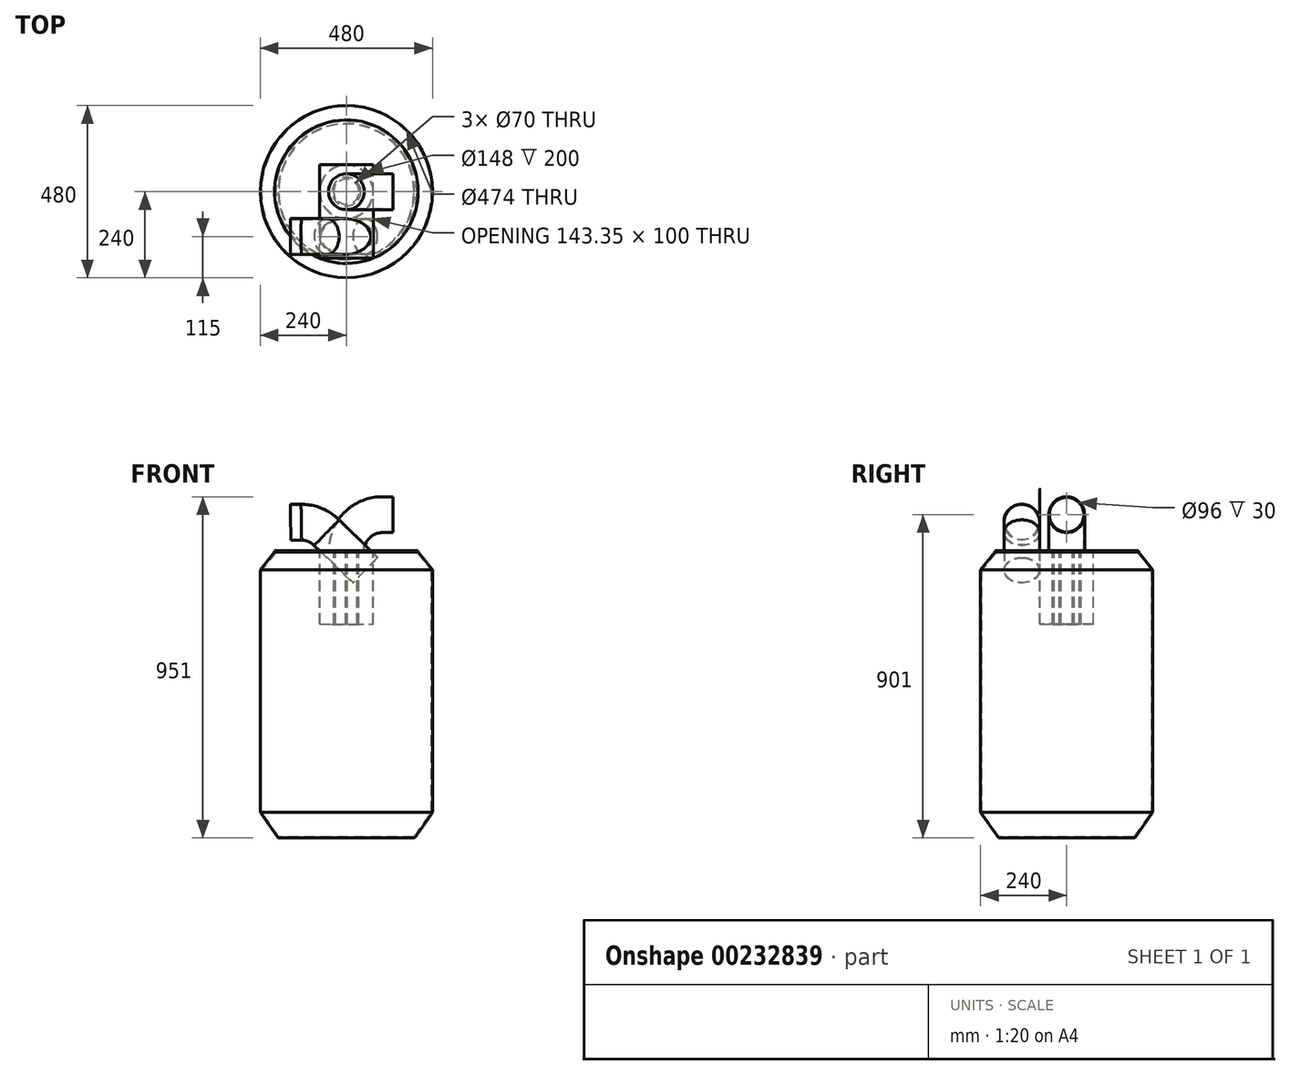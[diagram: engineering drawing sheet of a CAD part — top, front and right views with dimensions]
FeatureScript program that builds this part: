
annotation { "Feature Type Name" : "Feature", "Feature Type Description" : "" }
export const myFeature = defineFeature(function(context is Context, id is Id, definition is map)
    precondition{}
    {
        {
            assignVariable(context, id + "F0", {"name" : "FilterHeight", "anyValue" : 200});
        }
        {
            var Q0;
            Q0=qCreatedBy(makeId("Top.planeOp"),FACE);
            var sketch = newSketch(context, id + "F1", { "sketchPlane" : qUnion([Q0])});
            skCircle(sketch, "E0", {"center": v(0, 0) * mm, "radius": 200 * mm});
            skCircle(sketch, "E1", {"center": v(0, 0) * mm, "radius": 35 * mm});
            skSolve(sketch);
        }
        {
            var Q0;
            Q0=qSketchRegion(id+"F1",true);
            extrude(context, id + "F2", {"entities" : qUnion([Q0]), "depth" : 3 * mm});
        }
        {
            var Q0;
            Q0=makeQuery(id+"F2.opExtrude","CAP_FACE",FACE,{"disambiguationData":[OSD([sQuery(id+"F1.wireOp",EDGE,"E0"),sQuery(id+"F1.wireOp",EDGE,"E1")])],"isStart":true});
            var sketch = newSketch(context, id + "F3", { "sketchPlane" : qUnion([Q0])});
            skLineSegment(sketch, "E2.bottom", {"start": v(75, -75) * mm, "end": v(-75, -75) * mm});
            skLineSegment(sketch, "E2.top", {"start": v(75, 75) * mm, "end": v(-75, 75) * mm});
            skLineSegment(sketch, "E2.left", {"start": v(75, -75) * mm, "end": v(75, 75) * mm});
            skLineSegment(sketch, "E2.right", {"start": v(-75, -75) * mm, "end": v(-75, 75) * mm});
            skPoint(sketch, "E2.middle", {"position": v(0, 0) * mm});
            skCircle(sketch, "E3.0", {"center": v(0, 0) * mm, "radius": 35 * mm});
            skLineSegment(sketch, "E4.top", {"start": v(75, 185.4) * mm, "end": v(-75, 185.4) * mm});
            skLineSegment(sketch, "E4.left", {"start": v(75, 75) * mm, "end": v(75, 185.4) * mm});
            skLineSegment(sketch, "E4.right", {"start": v(-75, 75) * mm, "end": v(-75, 185.4) * mm});
            skSolve(sketch);
        }
        {
            var Q0;
            Q0=qSketchRegion(id+"F3",true);
            extrude(context, id + "F4", {"entities" : qUnion([Q0]), "depth" : 1 * mm});
        }
        {
            var Q0;
            Q0=makeQuery(id+"F4.opExtrude","CAP_FACE",FACE,{"disambiguationData":[OSD([sQuery(id+"F3.wireOp",EDGE,"E2.bottom"),sQuery(id+"F3.wireOp",EDGE,"E2.top"),sQuery(id+"F3.wireOp",EDGE,"E2.left"),sQuery(id+"F3.wireOp",EDGE,"E2.right"),sQuery(id+"F3.wireOp",EDGE,"E3.0")])],"isStart":false});
            var sketch = newSketch(context, id + "F5", { "sketchPlane" : qUnion([Q0])});
            skCircle(sketch, "E5", {"center": v(0, 37.5) * mm, "radius": 2.5 * mm});
            skCircle(sketch, "E6.1.0", {"center": v(-32.48, 18.75) * mm, "radius": 2.5 * mm});
            skCircle(sketch, "E6.2.0", {"center": v(-32.48, -18.75) * mm, "radius": 2.5 * mm});
            skCircle(sketch, "E6.3.0", {"center": v(0, -37.5) * mm, "radius": 2.5 * mm});
            skCircle(sketch, "E6.4.0", {"center": v(32.48, -18.75) * mm, "radius": 2.5 * mm});
            skCircle(sketch, "E6.5.0", {"center": v(32.48, 18.75) * mm, "radius": 2.5 * mm});
            skPoint(sketch, "E6.center", {"position": v(0, 0) * mm});
            skSolve(sketch);
        }
        {
            var Q0;
            Q0=qSketchRegion(id+"F5",true);
            extrude(context, id + "F6", {"entities" : qUnion([Q0]), "depth" : (getVariable(context, 'FilterHeight')) * mm});
        }
        {
            var Q0;
            Q0=makeQuery(id+"F6.opExtrude","CAP_FACE",FACE,{"disambiguationData":[OSD([sQuery(id+"F5.wireOp",EDGE,"E5")])],"isStart":false});
            var sketch = newSketch(context, id + "F7", { "sketchPlane" : qUnion([Q0])});
            skCircle(sketch, "E7", {"center": v(0, 0) * mm, "radius": 40 * mm});
            skSolve(sketch);
        }
        {
            var Q0;
            Q0=qSketchRegion(id+"F7",true);
            extrude(context, id + "F8", {"entities" : qUnion([Q0]), "depth" : 1 * mm});
        }
        {
            var Q0;
            Q0=makeQuery(id+"F4.opExtrude","CAP_FACE",FACE,{"disambiguationData":[OSD([sQuery(id+"F3.wireOp",EDGE,"E2.bottom"),sQuery(id+"F3.wireOp",EDGE,"E2.top"),sQuery(id+"F3.wireOp",EDGE,"E2.left"),sQuery(id+"F3.wireOp",EDGE,"E2.right"),sQuery(id+"F3.wireOp",EDGE,"E3.0")])],"isStart":false});
            var sketch = newSketch(context, id + "F9", { "sketchPlane" : qUnion([Q0])});
            skCircle(sketch, "E8", {"center": v(0, 0) * mm, "radius": 75 * mm});
            skCircle(sketch, "E9.0", {"center": v(0, 0) * mm, "radius": 74 * mm});
            skSolve(sketch);
        }
        {
            var Q0;
            Q0=qSketchRegion(id+"F9",true);
            extrude(context, id + "F10", {"entities" : qUnion([Q0]), "depth" : (getVariable(context, 'FilterHeight')) * mm});
        }
        {
            var Q0;
            Q0=makeQuery(id+"F2.opExtrude","CAP_FACE",FACE,{"disambiguationData":[OSD([sQuery(id+"F1.wireOp",EDGE,"E0"),sQuery(id+"F1.wireOp",EDGE,"E1")])],"isStart":false});
            var sketch = newSketch(context, id + "F11", { "sketchPlane" : qUnion([Q0])});
            skLineSegment(sketch, "E10.bottom", {"start": v(75, -75) * mm, "end": v(-75, -75) * mm});
            skLineSegment(sketch, "E10.top", {"start": v(75, 75) * mm, "end": v(-75, 75) * mm});
            skLineSegment(sketch, "E10.left", {"start": v(75, -75) * mm, "end": v(75, 75) * mm});
            skLineSegment(sketch, "E10.right", {"start": v(-75, -75) * mm, "end": v(-75, 75) * mm});
            skPoint(sketch, "E10.middle", {"position": v(0, 0) * mm});
            skCircle(sketch, "E11.0", {"center": v(0, 0) * mm, "radius": 35 * mm});
            skLineSegment(sketch, "E12.bottom", {"start": v(-75, -75) * mm, "end": v(75, -75) * mm});
            skLineSegment(sketch, "E12.top", {"start": v(-75, -185.4) * mm, "end": v(75, -185.4) * mm});
            skLineSegment(sketch, "E12.left", {"start": v(-75, -75) * mm, "end": v(-75, -185.4) * mm});
            skLineSegment(sketch, "E12.right", {"start": v(75, -75) * mm, "end": v(75, -185.4) * mm});
            skSolve(sketch);
        }
        {
            var Q0;
            Q0=qSketchRegion(id+"F11",true);
            extrude(context, id + "F12", {"entities" : qUnion([Q0]), "depth" : 1 * mm});
        }
        {
            var Q0;
            Q0=qCreatedBy(makeId("Front.planeOp"),FACE);
            var sketch = newSketch(context, id + "F13", { "sketchPlane" : qUnion([Q0])});
            skArc(sketch, "E13", {"start": v(100, 104) * mm, "mid": v(29.29, 74.71) * mm, "end": v(0, 4) * mm});
            skLineSegment(sketch, "E14", {"start": v(100, 104) * mm, "end": v(130, 104) * mm});
            skLineSegment(sketch, "E15", {"start": v(0, 4) * mm, "end": v(0, -27.41) * mm, "construction": true});
            skSolve(sketch);
        }
        {
            var Q0;
            Q0=makeQuery(id+"F12.opExtrude","CAP_FACE",FACE,{"disambiguationData":[OSD([sQuery(id+"F11.wireOp",EDGE,"E10.bottom"),sQuery(id+"F11.wireOp",EDGE,"E10.top"),sQuery(id+"F11.wireOp",EDGE,"E10.left"),sQuery(id+"F11.wireOp",EDGE,"E10.right"),sQuery(id+"F11.wireOp",EDGE,"E11.0")])],"isStart":false});
            var sketch = newSketch(context, id + "F14", { "sketchPlane" : qUnion([Q0])});
            skCircle(sketch, "E16", {"center": v(0, 0) * mm, "radius": 50 * mm});
            skCircle(sketch, "E17", {"center": v(0, 0) * mm, "radius": 48 * mm});
            skSolve(sketch);
        }
        {
            var Q0;
            Q0=makeQuery(id+"F14.imprint","IMPRINT",FACE,{"disambiguationData":[TD([[makeQuery(id+"F14.imprint","IMPRINT",EDGE,{"derivedFrom":sQuery(id+"F14.wireOp",EDGE,"E16")}),1.0]])]});
            var Q1;
            Q1=sQuery(id+"F13.wireOp",EDGE,"E13");
            var Q2;
            Q2=sQuery(id+"F13.wireOp",EDGE,"E14");
            sweep(context, id + "F15", {"profiles" : qUnion([Q0]), "path" : qUnion([Q1, Q2])});
        }
        {
            var Q0;
            Q0=makeQuery(id+"F2.opExtrude","CAP_FACE",FACE,{"disambiguationData":[OSD([sQuery(id+"F1.wireOp",EDGE,"E0"),sQuery(id+"F1.wireOp",EDGE,"E1")])],"isStart":false});
            var sketch = newSketch(context, id + "F16", { "sketchPlane" : qUnion([Q0])});
            skLineSegment(sketch, "E18", {"start": v(0, 0) * mm, "end": v(0, -207.17) * mm});
            skSolve(sketch);
        }
        {
            var Q0;
            Q0=sQuery(id+"F16.wireOp",EDGE,"E18");
            var Q1;
            Q1=makeQuery(id+"F12.opExtrude","CAP_VERTEX",VERTEX,{"disambiguationData":[OSD([sQuery(id+"F11.wireOp",EDGE,"E10.bottom"),sQuery(id+"F11.wireOp",EDGE,"E10.left")])],"isStart":false});
            cPlane(context, id + "F17", {"entities" : qUnion([Q0, Q1]), "cplaneType" : CPlaneType.LINE_ANGLE, "offset" : 25 * mm, "angle" : 45 * degree, "width" : 150 * mm, "height" : 150 * mm});
        }
        {
            var Q0;
            Q0=qCreatedBy(id+"F17.planeOp",FACE);
            var sketch = newSketch(context, id + "F18", { "sketchPlane" : qUnion([Q0])});
            skCircle(sketch, "E19", {"center": v(125, 0) * mm, "radius": 50 * mm});
            skSolve(sketch);
        }
        {
            var Q0;
            Q0=qSketchRegion(id+"F18",true);
            extrude(context, id + "F19", {"entities" : qUnion([Q0]), "operationType" : NewBodyOperationType.REMOVE, "endBound" : BoundingType.THROUGH_ALL, "oppositeDirection" : true, "depth" : 25 * mm, "hasSecondDirection" : true, "secondDirectionBound" : SecondDirectionBoundingType.THROUGH_ALL, "secondDirectionOppositeDirection" : false, "secondDirectionDepth" : 25 * mm});
        }
        {
            var Q0;
            Q0=qCreatedBy(id+"F17.planeOp",FACE);
            var sketch = newSketch(context, id + "F20", { "sketchPlane" : qUnion([Q0])});
            skCircle(sketch, "E20.0", {"center": v(125, 0) * mm, "radius": 50 * mm});
            skCircle(sketch, "E21", {"center": v(125, 0) * mm, "radius": 48 * mm});
            skSolve(sketch);
        }
        {
            var Q0;
            Q0=qSketchRegion(id+"F20",true);
            extrude(context, id + "F21", {"entities" : qUnion([Q0]), "endBound" : BoundingType.SYMMETRIC, "depth" : 150 * mm});
        }
        {
            var Q0;
            Q0=qCreatedBy(makeId("Front.planeOp"),FACE);
            cPlane(context, id + "F22", {"entities" : qUnion([Q0]), "cplaneType" : CPlaneType.OFFSET, "offset" : 125 * mm, "width" : 150 * mm, "height" : 150 * mm});
        }
        {
            var Q0;
            Q0=qCreatedBy(id+"F22.planeOp",FACE);
            var sketch = newSketch(context, id + "F23", { "sketchPlane" : qUnion([Q0])});
            skArc(sketch, "E22", {"start": v(-55.23, 53.78) * mm, "mid": v(-87.5, 75.42) * mm, "end": v(-125.59, 83.01) * mm});
            skLineSegment(sketch, "E23", {"start": v(-125.59, 83.01) * mm, "end": v(-155.59, 83.01) * mm});
            skLineSegment(sketch, "E24.0", {"start": v(-90.12, 17.96) * mm, "end": v(-20.35, 89.6) * mm, "construction": true});
            skLineSegment(sketch, "E25", {"start": v(-125.59, 83.01) * mm, "end": v(-125.59, -8.86) * mm, "construction": true});
            skSolve(sketch);
        }
        {
            var Q0;
            Q0=makeQuery(id+"F21.opExtrude","CAP_FACE",FACE,{"disambiguationData":[OSD([sQuery(id+"F20.wireOp",EDGE,"E20.0"),sQuery(id+"F20.wireOp",EDGE,"E21")])],"isStart":false});
            var sketch = newSketch(context, id + "F24", { "sketchPlane" : qUnion([Q0])});
            skCircle(sketch, "E26.0", {"center": v(125, 0) * mm, "radius": 50 * mm});
            skCircle(sketch, "E27.0", {"center": v(125, 0) * mm, "radius": 48 * mm});
            skSolve(sketch);
        }
        {
            var Q0;
            Q0=makeQuery(id+"F24.imprint","IMPRINT",FACE,{"disambiguationData":[TD([[makeQuery(id+"F24.imprint","IMPRINT",EDGE,{"derivedFrom":sQuery(id+"F24.wireOp",EDGE,"E26.0")}),1.0]])]});
            var Q1;
            Q1=sQuery(id+"F23.wireOp",EDGE,"E22");
            var Q2;
            Q2=sQuery(id+"F23.wireOp",EDGE,"E23");
            sweep(context, id + "F25", {"operationType" : NewBodyOperationType.ADD, "profiles" : qUnion([Q0]), "path" : qUnion([Q1, Q2])});
        }
        {
            var Q0;
            Q0=qCreatedBy(makeId("Right.planeOp"),FACE);
            var sketch = newSketch(context, id + "F26", { "sketchPlane" : qUnion([Q0])});
            skLineSegment(sketch, "E28", {"start": v(-200, 0) * mm, "end": v(-240, -49.57) * mm});
            skLineSegment(sketch, "E29", {"start": v(-240, -49.57) * mm, "end": v(-240, -725.99) * mm});
            skLineSegment(sketch, "E30", {"start": v(-240, -725.99) * mm, "end": v(-190, -797) * mm});
            skLineSegment(sketch, "E31", {"start": v(-190, -797) * mm, "end": v(0, -797) * mm});
            skLineSegment(sketch, "E32", {"start": v(-200, 0) * mm, "end": v(-200, 3) * mm, "construction": true});
            skLineSegment(sketch, "E33.0", {"start": v(-188.44, -794) * mm, "end": v(0, -794) * mm});
            skLineSegment(sketch, "E33.1", {"start": v(-237, -725.04) * mm, "end": v(-188.44, -794) * mm});
            skLineSegment(sketch, "E33.2", {"start": v(-237, -50.63) * mm, "end": v(-237, -725.04) * mm});
            skLineSegment(sketch, "E33.3", {"start": v(-196.15, 0) * mm, "end": v(-237, -50.63) * mm});
            skLineSegment(sketch, "E34", {"start": v(0, -797) * mm, "end": v(0, -794) * mm});
            skLineSegment(sketch, "E35", {"start": v(-196.15, 0) * mm, "end": v(-200, 0) * mm});
            skSolve(sketch);
        }
        {
            var Q0;
            Q0=qSketchRegion(id+"F26",true);
            var Q1;
            Q1=makeQuery(id+"F10.opExtrude","CAP_EDGE",EDGE,{"disambiguationData":[OSD([sQuery(id+"F9.wireOp",EDGE,"E8")])],"isStart":false});
            revolve(context, id + "F27", {"entities" : qUnion([Q0]), "axis" : qUnion([Q1]), "revolveType" : RevolveType.FULL});
        }
    });
